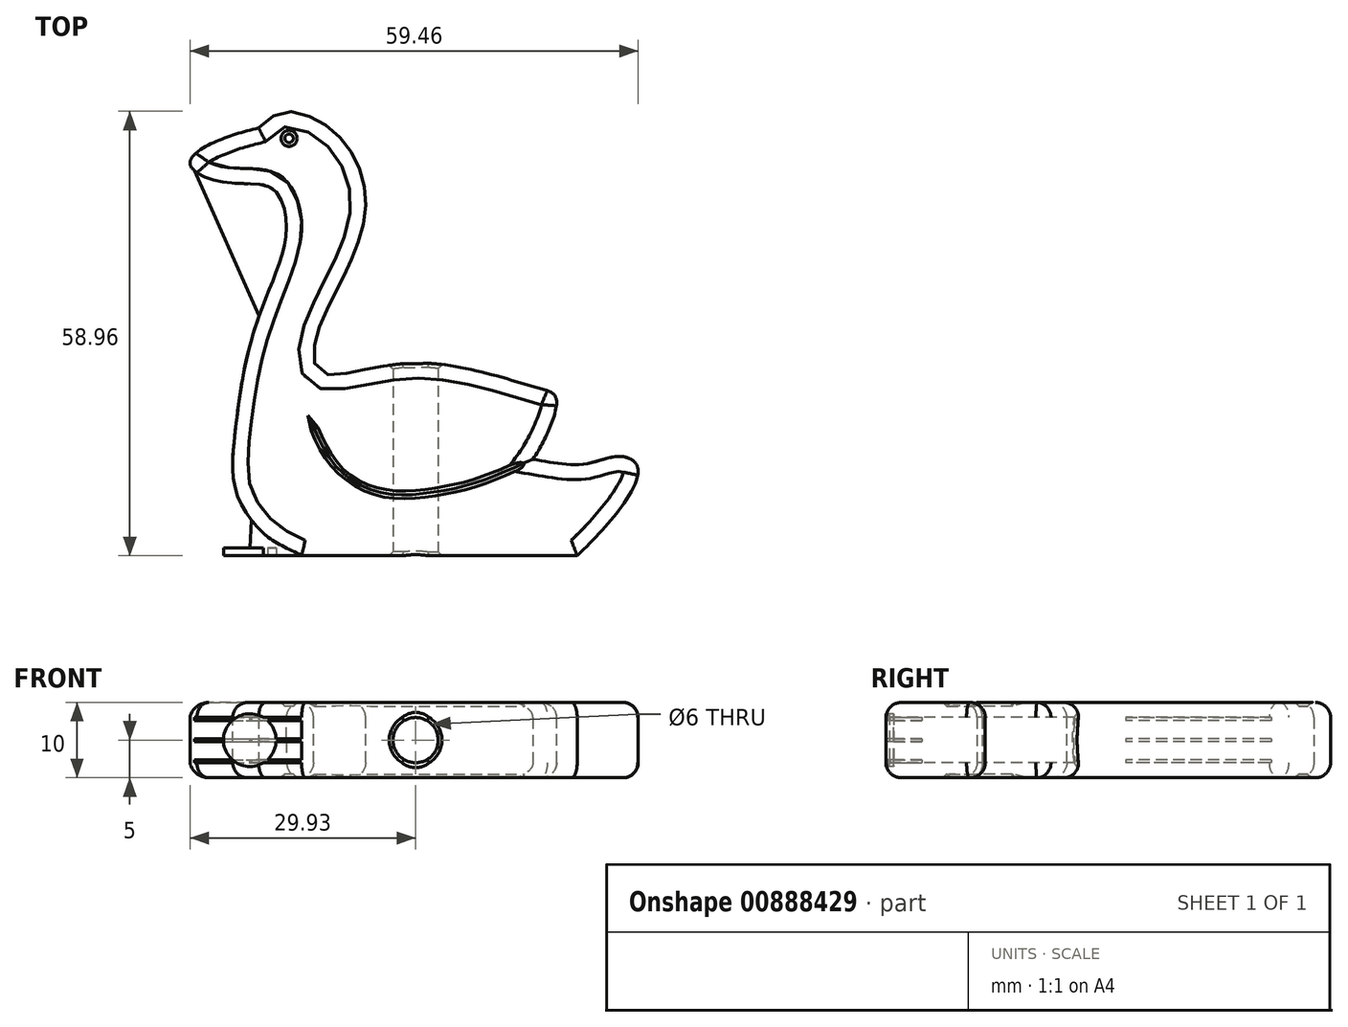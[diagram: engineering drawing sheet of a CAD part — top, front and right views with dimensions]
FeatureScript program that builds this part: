
annotation { "Feature Type Name" : "Feature", "Feature Type Description" : "" }
export const myFeature = defineFeature(function(context is Context, id is Id, definition is map)
    precondition{}
    {
        {
            var Q0;
            Q0=qCreatedBy(makeId("Top.planeOp"),FACE);
            cPlane(context, id + "F0", {"entities" : qUnion([Q0]), "cplaneType" : CPlaneType.OFFSET, "offset" : 5 * mm, "width" : 150 * mm, "height" : 150 * mm});
        }
        {
            var Q0;
            Q0=qCreatedBy(makeId("Top.planeOp"),FACE);
            var sketch = newSketch(context, id + "F1", { "sketchPlane" : qUnion([Q0])});
            skLineSegment(sketch, "E0", {"start": v(19.88, 4.87) * mm, "end": v(56.44, 4.87) * mm});
            skFitSpline(sketch, "E1", {"points": [v(56.44, 4.87) * mm, v(64.51, 16.27) * mm, v(62.19, 18.02) * mm, v(57.44, 17.02) * mm, v(50.57, 17.65) * mm], "startDerivative": vector(34.05, 31.78) * mm, "endDerivative": vector(-28.76, 4.89) * mm});
            skFitSpline(sketch, "E2", {"points": [v(50.57, 17.65) * mm, v(53.7, 25.36) * mm, v(51.1, 27.15) * mm, v(36.15, 30.4) * mm, v(24.7, 28.9) * mm, v(21.97, 29.53) * mm, v(21.8, 33.8) * mm, v(26.33, 43.78) * mm, v(28.28, 53.3) * mm, v(23.98, 61.3) * mm, v(17.78, 63.83) * mm, v(14.16, 61.63) * mm], "startDerivative": vector(31.71, 43.8) * mm, "endDerivative": vector(-72.4, -60.82) * mm});
            skFitSpline(sketch, "E3", {"points": [v(14.16, 61.63) * mm, v(5.07, 56.94) * mm, v(8.7, 54.58) * mm, v(14.16, 54.15) * mm, v(16.52, 53.08) * mm, v(17.83, 47.63) * mm, v(13.66, 34.98) * mm, v(11.1, 21.66) * mm, v(11.32, 12.95) * mm, v(14.83, 7.81) * mm, v(19.88, 4.87) * mm], "startDerivative": vector(-127.98, -30.37) * mm, "endDerivative": vector(111.6, -56.19) * mm});
            skSolve(sketch);
        }
        {
            var Q0;
            Q0=makeQuery(id+"F1.imprint","IMPRINT",FACE,{"disambiguationData":[TD([[makeQuery(id+"F1.imprint","IMPRINT",EDGE,{"derivedFrom":sQuery(id+"F1.wireOp",EDGE,"E0")}),1.0]])]});
            extrude(context, id + "F2", {"entities" : qUnion([Q0]), "depth" : 10 * mm, "offsetDistance" : 25 * mm});
        }
        {
            var Q0;
            Q0=makeQuery(id+"F2.opExtrude","CAP_FACE",FACE,{"disambiguationData":[OSD([sQuery(id+"F1.wireOp",EDGE,"E0"),sQuery(id+"F1.wireOp",EDGE,"E1"),sQuery(id+"F1.wireOp",EDGE,"E2"),sQuery(id+"F1.wireOp",EDGE,"E3")])],"isStart":false});
            fillet(context, id + "F3", {"entities" : qUnion([Q0]), "radius" : 2 * mm, "tangentPropagation" : true, "allowEdgeOverflow" : false});
        }
        {
            var Q0;
            Q0=makeQuery(id+"F2.opExtrude","CAP_FACE",FACE,{"disambiguationData":[OSD([sQuery(id+"F1.wireOp",EDGE,"E0"),sQuery(id+"F1.wireOp",EDGE,"E1"),sQuery(id+"F1.wireOp",EDGE,"E2"),sQuery(id+"F1.wireOp",EDGE,"E3")])],"isStart":true});
            fillet(context, id + "F4", {"entities" : qUnion([Q0]), "radius" : 2 * mm, "tangentPropagation" : true, "allowEdgeOverflow" : false});
        }
        {
            var Q0;
            Q0=makeQuery(id+"F2.opExtrude","CAP_FACE",FACE,{"disambiguationData":[OSD([sQuery(id+"F1.wireOp",EDGE,"E0"),sQuery(id+"F1.wireOp",EDGE,"E1"),sQuery(id+"F1.wireOp",EDGE,"E2"),sQuery(id+"F1.wireOp",EDGE,"E3")])],"isStart":false});
            var sketch = newSketch(context, id + "F5", { "sketchPlane" : qUnion([Q0])});
            skFitSpline(sketch, "E4", {"points": [v(50.57, 17.65) * mm, v(36.86, 13.22) * mm, v(21.58, 21.68) * mm], "startDerivative": vector(-44.74, -19.98) * mm, "endDerivative": vector(-25.32, 54.36) * mm});
            skFitSpline(sketch, "E5.0", {"points": [v(50.37, 18.1) * mm, v(48.5, 17.27) * mm, v(45.42, 15.95) * mm, v(42.6, 14.95) * mm, v(40.64, 14.4) * mm, v(39.22, 14.1) * mm, v(38.01, 13.89) * mm, v(36.99, 13.74) * mm, v(35.9, 13.6) * mm, v(34.49, 13.45) * mm, v(32.7, 13.43) * mm, v(30.86, 13.64) * mm, v(28.4, 14.38) * mm, v(25.34, 16.36) * mm, v(23.07, 19.66) * mm, v(22.03, 21.89) * mm]});
            skFitSpline(sketch, "E6.0", {"points": [v(50.78, 17.2) * mm, v(48.9, 16.36) * mm, v(45.8, 15.03) * mm, v(42.91, 14) * mm, v(40.88, 13.44) * mm, v(39.4, 13.11) * mm, v(38.17, 12.9) * mm, v(37.12, 12.75) * mm, v(36.03, 12.6) * mm, v(34.55, 12.45) * mm, v(32.65, 12.43) * mm, v(30.66, 12.66) * mm, v(28.63, 13.26) * mm, v(26.6, 14.34) * mm, v(24, 16.54) * mm, v(22.2, 19.16) * mm, v(21.13, 21.47) * mm]});
            skLineSegment(sketch, "E7", {"start": v(50.37, 18.1) * mm, "end": v(50.78, 17.2) * mm});
            skLineSegment(sketch, "E8", {"start": v(21.58, 21.68) * mm, "end": v(20.74, 23.49) * mm, "construction": true});
            skLineSegment(sketch, "E9", {"start": v(22.03, 21.89) * mm, "end": v(20.74, 23.49) * mm});
            skLineSegment(sketch, "E10", {"start": v(21.13, 21.47) * mm, "end": v(20.74, 23.49) * mm});
            skCircle(sketch, "E11", {"center": v(18.22, 60.24) * mm, "radius": 1.06 * mm});
            skSolve(sketch);
        }
        {
            var Q0;
            {var subQ10=sQuery(id+"F5.wireOp",EDGE,"E9");Q0=makeQuery(id+"F5.imprint","IMPRINT",FACE,{"disambiguationData":[TD([[makeQuery(id+"F5.imprint","IMPRINT",EDGE,{"derivedFrom":subQ10}),1.0]])]});}
            var Q1;
            {var subQ0=sQuery(id+"F5.wireOp",EDGE,"E7");var subQ1=sQuery(id+"F5.wireOp",EDGE,"E4");var subQ2=makeQuery(id+"F5.imprint","INTERSECT",VERTEX,{"derivedFrom":[subQ1,subQ0]});Q1=makeQuery(id+"F5.imprint","IMPRINT",FACE,{"disambiguationData":[TD([[makeQuery(id+"F5.imprint","IMPRINT",EDGE,{"disambiguationData":[TD([[subQ2,-1.0]])],"derivedFrom":subQ0}),-1.0]])]});}
            var Q2;
            {var subQ0=sQuery(id+"F5.wireOp",EDGE,"E7");var subQ10=sQuery(id+"F5.wireOp",EDGE,"E4");var subQ12=makeQuery(id+"F5.imprint","INTERSECT",VERTEX,{"derivedFrom":[subQ10,subQ0]});Q2=makeQuery(id+"F5.imprint","IMPRINT",FACE,{"disambiguationData":[TD([[makeQuery(id+"F5.imprint","IMPRINT",EDGE,{"disambiguationData":[TD([[subQ12,1.0]])],"derivedFrom":subQ0}),-1.0]])]});}
            extrude(context, id + "F6", {"entities" : qUnion([Q0, Q1, Q2]), "oppositeDirection" : true, "depth" : 2 * mm, "offsetDistance" : 25 * mm, "hasDraft" : true, "draftAngle" : 45 * degree, "draftPullDirection" : true});
        }
        {
            var Q0;
            Q0=makeQuery(id+"F6.opExtrude","SWEPT_BODY",BODY,{"disambiguationData":[OSD([sQuery(id+"F5.wireOp",EDGE,"E5.0"),sQuery(id+"F5.wireOp",EDGE,"E6.0"),sQuery(id+"F5.wireOp",EDGE,"E7"),sQuery(id+"F5.wireOp",EDGE,"E9"),sQuery(id+"F5.wireOp",EDGE,"E10")])]});
            var Q1;
            Q1=qCreatedBy(id+"F0.planeOp",FACE);
            mirror(context, id + "F7", {"operationType" : NewBodyOperationType.REMOVE, "entities" : qUnion([Q0]), "mirrorPlane" : qUnion([Q1])});
        }
        {
            var Q0;
            Q0=makeQuery(id+"F6.opExtrude","SWEPT_BODY",BODY,{"disambiguationData":[OSD([sQuery(id+"F5.wireOp",EDGE,"E5.0"),sQuery(id+"F5.wireOp",EDGE,"E6.0"),sQuery(id+"F5.wireOp",EDGE,"E7"),sQuery(id+"F5.wireOp",EDGE,"E9"),sQuery(id+"F5.wireOp",EDGE,"E10")])]});
            var Q1;
            Q1=makeQuery(id+"F2.opExtrude","SWEPT_BODY",BODY,{"disambiguationData":[OSD([sQuery(id+"F1.wireOp",EDGE,"E0"),sQuery(id+"F1.wireOp",EDGE,"E1"),sQuery(id+"F1.wireOp",EDGE,"E2"),sQuery(id+"F1.wireOp",EDGE,"E3")])]});
            booleanBodies(context, id + "F8", {"operationType" : BooleanOperationType.SUBTRACTION, "tools" : qUnion([Q0]), "targets" : qUnion([Q1])});
        }
        {
            var Q0;
            Q0=makeQuery(id+"F5.imprint","IMPRINT",FACE,{"disambiguationData":[TD([[makeQuery(id+"F5.imprint","IMPRINT",EDGE,{"derivedFrom":sQuery(id+"F5.wireOp",EDGE,"E11")}),1.0]])]});
            extrude(context, id + "F9", {"entities" : qUnion([Q0]), "oppositeDirection" : true, "depth" : 0.5 * mm, "offsetDistance" : 25 * mm, "hasDraft" : true, "draftAngle" : 45 * degree, "draftPullDirection" : true});
        }
        {
            var Q0;
            Q0=makeQuery(id+"F9.opExtrude","SWEPT_BODY",BODY,{"disambiguationData":[OSD([sQuery(id+"F5.wireOp",EDGE,"E11")])]});
            var Q1;
            Q1=qCreatedBy(id+"F0.planeOp",FACE);
            mirror(context, id + "F10", {"operationType" : NewBodyOperationType.REMOVE, "entities" : qUnion([Q0]), "mirrorPlane" : qUnion([Q1])});
        }
        {
            var Q0;
            Q0=makeQuery(id+"F9.opExtrude","SWEPT_BODY",BODY,{"disambiguationData":[OSD([sQuery(id+"F5.wireOp",EDGE,"E11")])]});
            var Q1;
            Q1=makeQuery(id+"F2.opExtrude","SWEPT_BODY",BODY,{"disambiguationData":[OSD([sQuery(id+"F1.wireOp",EDGE,"E0"),sQuery(id+"F1.wireOp",EDGE,"E1"),sQuery(id+"F1.wireOp",EDGE,"E2"),sQuery(id+"F1.wireOp",EDGE,"E3")])]});
            booleanBodies(context, id + "F11", {"operationType" : BooleanOperationType.SUBTRACTION, "tools" : qUnion([Q0]), "targets" : qUnion([Q1])});
        }
        {
            var Q0;
            Q0=qCreatedBy(id+"F0.planeOp",FACE);
            var sketch = newSketch(context, id + "F12", { "sketchPlane" : qUnion([Q0])});
            skLineSegment(sketch, "E12", {"start": v(5.22, 56.9) * mm, "end": v(14.51, 36.12) * mm});
            skLineSegment(sketch, "E13", {"start": v(5.22, 56.9) * mm, "end": v(19.05, 54.23) * mm});
            skLineSegment(sketch, "E14", {"start": v(19.05, 54.23) * mm, "end": v(19.5, 43.79) * mm});
            skLineSegment(sketch, "E15", {"start": v(19.5, 43.79) * mm, "end": v(16.12, 15.37) * mm});
            skLineSegment(sketch, "E16", {"start": v(16.12, 15.37) * mm, "end": v(19.5, 8.97) * mm});
            skLineSegment(sketch, "E17", {"start": v(19.5, 8.97) * mm, "end": v(19.88, 4.87) * mm});
            skLineSegment(sketch, "E18", {"start": v(19.88, 4.87) * mm, "end": v(13, 4.87) * mm});
            skLineSegment(sketch, "E19", {"start": v(13, 4.87) * mm, "end": v(14.51, 36.12) * mm});
            skSolve(sketch);
        }
        {
            var Q0;
            Q0=makeQuery(id+"F12.imprint","IMPRINT",FACE,{"disambiguationData":[TD([[makeQuery(id+"F12.imprint","IMPRINT",EDGE,{"derivedFrom":sQuery(id+"F12.wireOp",EDGE,"E12")}),1.0]])]});
            extrude(context, id + "F13", {"entities" : qUnion([Q0]), "depth" : 3 * mm, "offsetDistance" : 25 * mm, "hasSecondDirection" : true, "secondDirectionOppositeDirection" : false, "secondDirectionDepth" : 2.6 * mm});
        }
        {
            var Q0;
            Q0=makeQuery(id+"F2.opExtrude","SWEPT_FACE",FACE,{"disambiguationData":[OSD([sQuery(id+"F1.wireOp",EDGE,"E0")])]});
            var sketch = newSketch(context, id + "F14", { "sketchPlane" : qUnion([Q0])});
            skCircle(sketch, "E20", {"center": v(35, 5) * mm, "radius": 3 * mm});
            skCircle(sketch, "E21", {"center": v(13, 5) * mm, "radius": 3.5 * mm});
            skSolve(sketch);
        }
        {
            var Q0;
            {var subQ0=sQuery(id+"F14.wireOp",EDGE,"E20");var subQ1=sQuery(id+"F1.wireOp",EDGE,"E0");var subQ2=makeQuery(id+"F2.opExtrude","SWEPT_FACE",FACE,{"disambiguationData":[OSD([subQ1])]});var subQ3=makeQuery(id+"F14.imprint","INTERSECT",VERTEX,{"derivedFrom":[makeQuery(id+"F3.opFillet","BLEND_EDGE",EDGE,{"blendedFrom":[makeQuery(id+"F2.opExtrude","CAP_EDGE",EDGE,{"disambiguationData":[OSD([subQ1])],"isStart":false}),subQ2],"blendedInto":[subQ2]}),subQ0]});Q0=makeQuery(id+"F14.imprint","IMPRINT",FACE,{"disambiguationData":[TD([[makeQuery(id+"F14.imprint","IMPRINT",EDGE,{"disambiguationData":[TD([[subQ3,-1.0]])],"derivedFrom":subQ0}),1.0]])]});}
            extrude(context, id + "F15", {"entities" : qUnion([Q0]), "operationType" : NewBodyOperationType.REMOVE, "oppositeDirection" : true, "depth" : 30 * mm, "offsetDistance" : 25 * mm});
        }
        {
            var Q0;
            Q0=makeQuery(id+"F15.boolean.opBoolean","COPY",EDGE,{"disambiguationData":[OD(0.0)],"derivedFrom":makeQuery(id+"F15.opExtrude","CAP_EDGE",EDGE,{"disambiguationData":[OSD([sQuery(id+"F14.wireOp",EDGE,"E20")])],"isStart":true})});
            chamfer(context, id + "F16", {"entities" : qUnion([Q0]), "width" : 0.5 * mm, "tangentPropagation" : true});
        }
        {
            var Q0;
            Q0=makeQuery(id+"F15.boolean.opBoolean","INTERSECT",EDGE,{"disambiguationData":[OD(1.0)],"derivedFrom":[makeQuery(id+"F2.opExtrude","SWEPT_FACE",FACE,{"disambiguationData":[OSD([sQuery(id+"F1.wireOp",EDGE,"E2")])]}),makeQuery(id+"F15.opExtrude","SWEPT_FACE",FACE,{"disambiguationData":[OSD([sQuery(id+"F14.wireOp",EDGE,"E20")])]})]});
            var Q1;
            Q1=makeQuery(id+"F15.boolean.opBoolean","INTERSECT",EDGE,{"disambiguationData":[OD(0.0)],"derivedFrom":[makeQuery(id+"F2.opExtrude","SWEPT_FACE",FACE,{"disambiguationData":[OSD([sQuery(id+"F1.wireOp",EDGE,"E2")])]}),makeQuery(id+"F15.opExtrude","SWEPT_FACE",FACE,{"disambiguationData":[OSD([sQuery(id+"F14.wireOp",EDGE,"E20")])]})]});
            chamfer(context, id + "F17", {"entities" : qUnion([Q0, Q1]), "width" : 0.5 * mm, "tangentPropagation" : true});
        }
        {
            var Q0;
            Q0=makeQuery(id+"F13.opExtrude","SWEPT_BODY",BODY,{"disambiguationData":[OSD([sQuery(id+"F12.wireOp",EDGE,"E12"),sQuery(id+"F12.wireOp",EDGE,"E13"),sQuery(id+"F12.wireOp",EDGE,"E14"),sQuery(id+"F12.wireOp",EDGE,"E15"),sQuery(id+"F12.wireOp",EDGE,"E16"),sQuery(id+"F12.wireOp",EDGE,"E17"),sQuery(id+"F12.wireOp",EDGE,"E18"),sQuery(id+"F12.wireOp",EDGE,"E19")])]});
            var Q1;
            Q1=qCreatedBy(id+"F0.planeOp",FACE);
            mirror(context, id + "F18", {"operationType" : NewBodyOperationType.ADD, "entities" : qUnion([Q0]), "mirrorPlane" : qUnion([Q1])});
        }
        {
            var Q0;
            Q0=makeQuery(id+"F12.imprint","IMPRINT",FACE,{"disambiguationData":[TD([[makeQuery(id+"F12.imprint","IMPRINT",EDGE,{"derivedFrom":sQuery(id+"F12.wireOp",EDGE,"E12")}),1.0]])]});
            extrude(context, id + "F19", {"entities" : qUnion([Q0]), "operationType" : NewBodyOperationType.ADD, "depth" : 0.2 * mm, "offsetDistance" : 25 * mm, "hasSecondDirection" : true, "secondDirectionOppositeDirection" : true, "secondDirectionDepth" : 0.2 * mm});
        }
        {
            var Q0;
            Q0=makeQuery(id+"F14.imprint","IMPRINT",FACE,{"disambiguationData":[TD([[makeQuery(id+"F14.imprint","IMPRINT",EDGE,{"derivedFrom":sQuery(id+"F14.wireOp",EDGE,"E21")}),1.0]])]});
            extrude(context, id + "F20", {"entities" : qUnion([Q0]), "operationType" : NewBodyOperationType.ADD, "oppositeDirection" : true, "depth" : 1 * mm, "offsetDistance" : 25 * mm});
        }
    });
